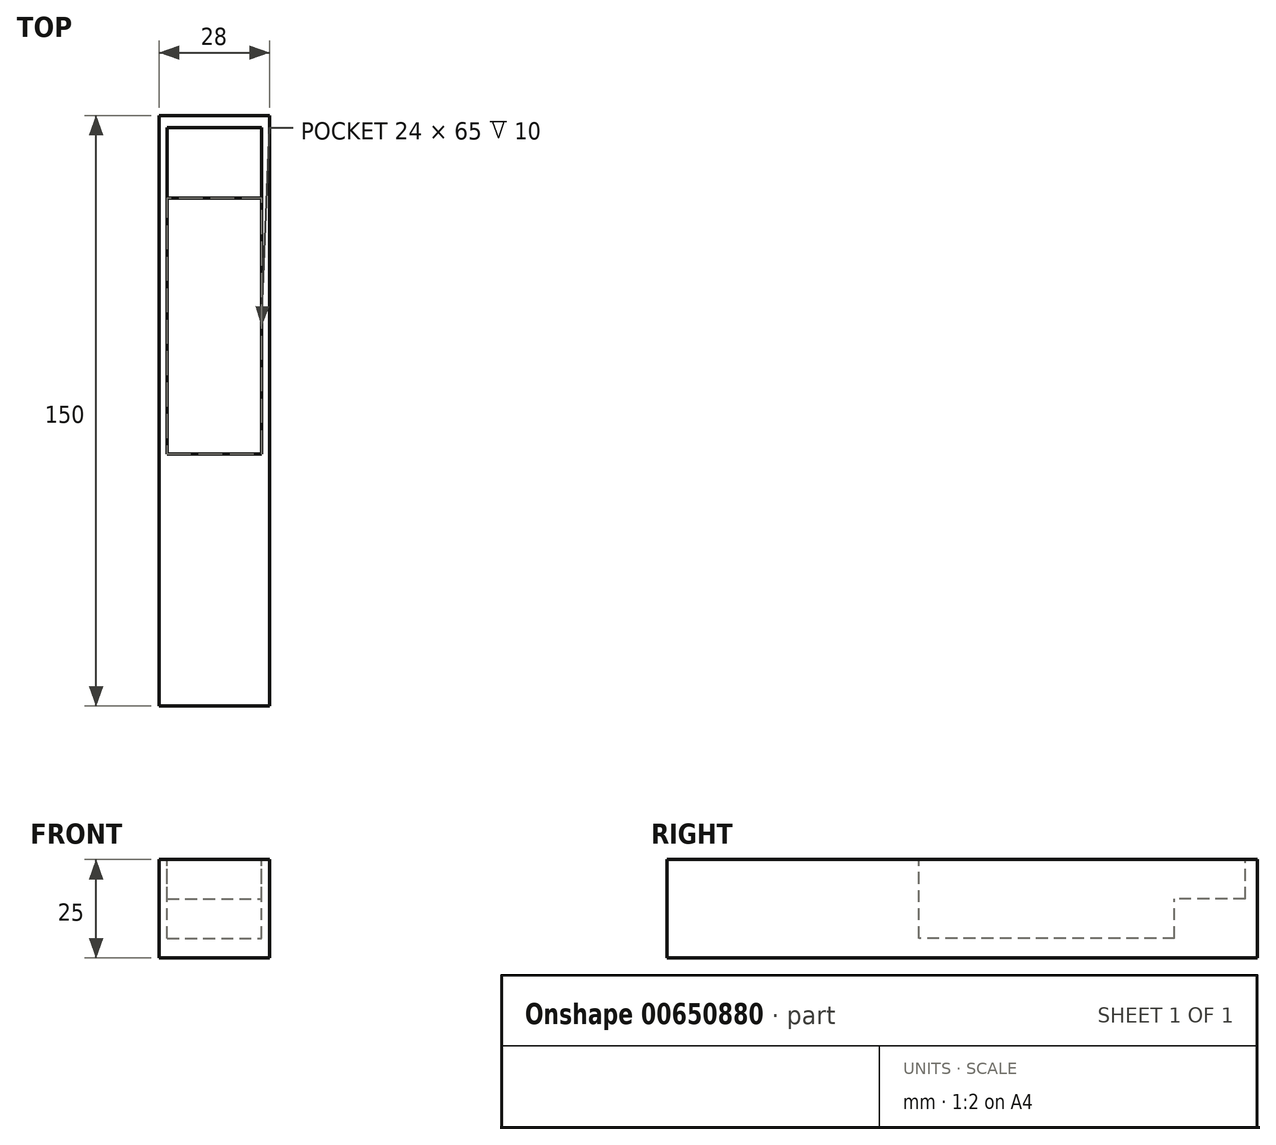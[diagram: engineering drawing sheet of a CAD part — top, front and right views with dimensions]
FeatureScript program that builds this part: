
annotation { "Feature Type Name" : "Feature", "Feature Type Description" : "" }
export const myFeature = defineFeature(function(context is Context, id is Id, definition is map)
    precondition{}
    {
        {
            var Q0;
            Q0=qCreatedBy(makeId("Front.planeOp"),FACE);
            var sketch = newSketch(context, id + "F0", { "sketchPlane" : qUnion([Q0])});
            skLineSegment(sketch, "E0.bottom", {"start": v(0, 0) * mm, "end": v(28, 0) * mm});
            skLineSegment(sketch, "E0.top", {"start": v(0, 25) * mm, "end": v(28, 25) * mm});
            skLineSegment(sketch, "E0.left", {"start": v(0, 0) * mm, "end": v(0, 25) * mm});
            skLineSegment(sketch, "E0.right", {"start": v(28, 0) * mm, "end": v(28, 25) * mm});
            skSolve(sketch);
        }
        {
            var Q0;
            Q0=makeQuery(id+"F0.imprint","IMPRINT",FACE,{"disambiguationData":[TD([[makeQuery(id+"F0.imprint","IMPRINT",EDGE,{"derivedFrom":sQuery(id+"F0.wireOp",EDGE,"E0.bottom")}),1.0]])]});
            extrude(context, id + "F1", {"entities" : qUnion([Q0]), "depth" : 150 * mm, "offsetDistance" : 25 * mm});
        }
        {
            var Q0;
            Q0=makeQuery(id+"F1.opExtrude","SWEPT_FACE",FACE,{"disambiguationData":[OSD([sQuery(id+"F0.wireOp",EDGE,"E0.top")])]});
            var sketch = newSketch(context, id + "F2", { "sketchPlane" : qUnion([Q0])});
            skLineSegment(sketch, "E1.bottom", {"start": v(2, -3) * mm, "end": v(26, -3) * mm});
            skLineSegment(sketch, "E1.top", {"start": v(2, -21) * mm, "end": v(26, -21) * mm});
            skLineSegment(sketch, "E1.left", {"start": v(2, -3) * mm, "end": v(2, -21) * mm});
            skLineSegment(sketch, "E1.right", {"start": v(26, -3) * mm, "end": v(26, -21) * mm});
            skSolve(sketch);
        }
        {
            var Q0;
            Q0=makeQuery(id+"F2.imprint","IMPRINT",FACE,{"disambiguationData":[TD([[makeQuery(id+"F2.imprint","IMPRINT",EDGE,{"derivedFrom":sQuery(id+"F2.wireOp",EDGE,"E1.bottom")}),-1.0]])]});
            extrude(context, id + "F3", {"entities" : qUnion([Q0]), "operationType" : NewBodyOperationType.REMOVE, "oppositeDirection" : true, "depth" : 10 * mm, "offsetDistance" : 25 * mm});
        }
        {
            var Q0;
            Q0=makeQuery(id+"F1.opExtrude","SWEPT_FACE",FACE,{"disambiguationData":[OSD([sQuery(id+"F0.wireOp",EDGE,"E0.top")])]});
            var sketch = newSketch(context, id + "F4", { "sketchPlane" : qUnion([Q0])});
            skLineSegment(sketch, "E2.bottom", {"start": v(2, -21) * mm, "end": v(26, -21) * mm});
            skLineSegment(sketch, "E2.top", {"start": v(2, -86) * mm, "end": v(26, -86) * mm});
            skLineSegment(sketch, "E2.left", {"start": v(2, -21) * mm, "end": v(2, -86) * mm});
            skLineSegment(sketch, "E2.right", {"start": v(26, -21) * mm, "end": v(26, -86) * mm});
            skSolve(sketch);
        }
        {
            var Q0;
            Q0=makeQuery(id+"F4.imprint","IMPRINT",FACE,{"disambiguationData":[TD([[makeQuery(id+"F4.imprint","IMPRINT",EDGE,{"derivedFrom":sQuery(id+"F4.wireOp",EDGE,"E2.bottom")}),-1.0]])]});
            extrude(context, id + "F5", {"entities" : qUnion([Q0]), "operationType" : NewBodyOperationType.REMOVE, "oppositeDirection" : true, "depth" : 20 * mm, "offsetDistance" : 25 * mm});
        }
    });
